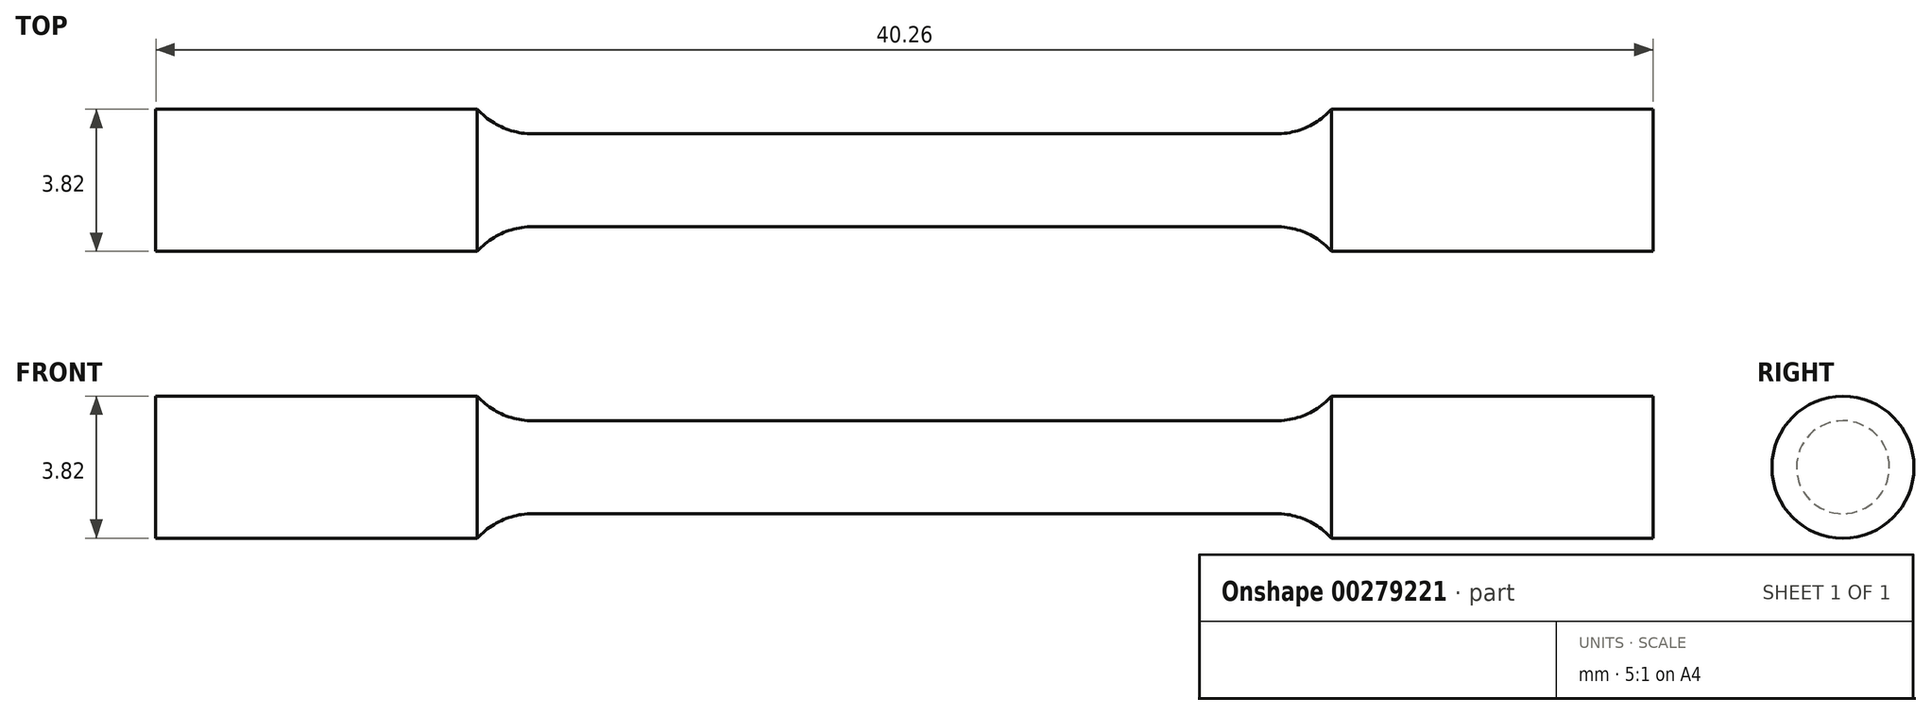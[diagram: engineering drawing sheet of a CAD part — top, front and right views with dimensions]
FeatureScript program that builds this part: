
annotation { "Feature Type Name" : "Feature", "Feature Type Description" : "" }
export const myFeature = defineFeature(function(context is Context, id is Id, definition is map)
    precondition{}
    {
        {
            var Q0;
            Q0=qCreatedBy(makeId("Front.planeOp"),FACE);
            var sketch = newSketch(context, id + "F0", { "sketchPlane" : qUnion([Q0])});
            skLineSegment(sketch, "E0", {"start": v(0, 1.25) * mm, "end": v(10, 1.25) * mm});
            skArc(sketch, "E1", {"start": v(10, 1.25) * mm, "mid": v(10.81, 1.42) * mm, "end": v(11.48, 1.9) * mm});
            skLineSegment(sketch, "E2", {"start": v(11.48, 1.9) * mm, "end": v(20.13, 1.9) * mm});
            skLineSegment(sketch, "E3", {"start": v(20.13, 1.9) * mm, "end": v(20.13, 0) * mm});
            skLineSegment(sketch, "E4.MirrorCS", {"start": v(0, 1.25) * mm, "end": v(-10, 1.25) * mm});
            skLineSegment(sketch, "E5.MirrorCS", {"start": v(-20.13, 1.9) * mm, "end": v(-20.13, 0) * mm});
            skLineSegment(sketch, "E6.MirrorCS", {"start": v(-11.48, 1.9) * mm, "end": v(-20.13, 1.9) * mm});
            skArc(sketch, "E7.MirrorCS", {"start": v(-10, 1.25) * mm, "mid": v(-10.81, 1.42) * mm, "end": v(-11.48, 1.9) * mm});
            skLineSegment(sketch, "E8", {"start": v(-20.13, 0) * mm, "end": v(20.13, 0) * mm});
            skSolve(sketch);
        }
        {
            var Q0;
            Q0 = qSketchRegion(id + "F0", true);
            var Q1;
            Q1=sQuery(id+"F0.wireOp",EDGE,"E8");
            revolve(context, id + "F1", {"entities" : qUnion([Q0]), "axis" : qUnion([Q1]), "revolveType" : RevolveType.FULL});
        }
    });
